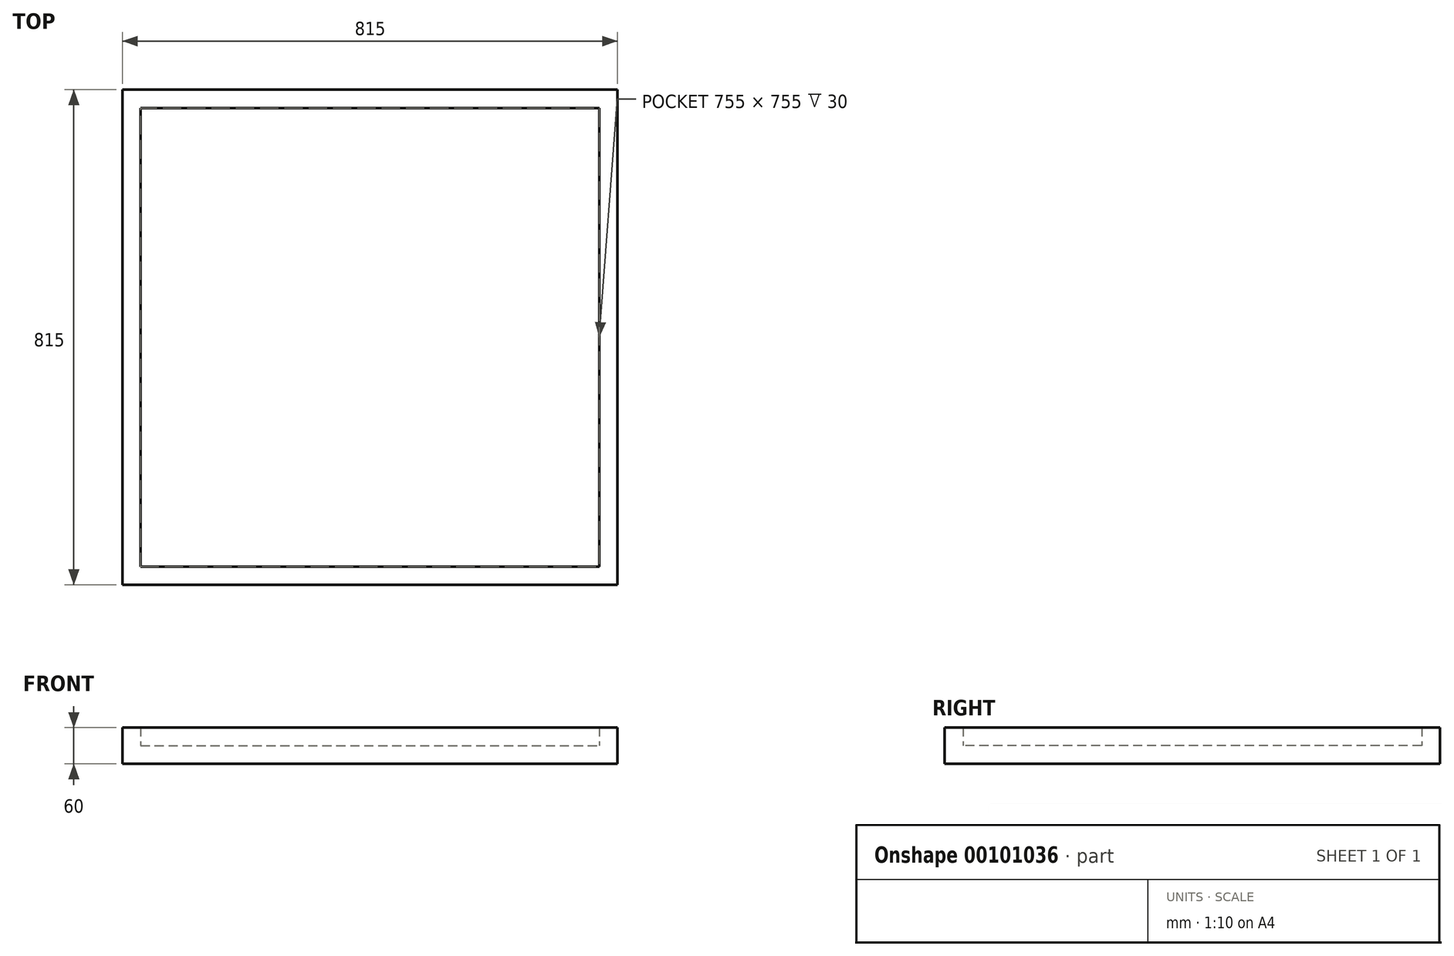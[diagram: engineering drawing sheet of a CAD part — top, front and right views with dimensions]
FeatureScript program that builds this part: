
annotation { "Feature Type Name" : "Feature", "Feature Type Description" : "" }
export const myFeature = defineFeature(function(context is Context, id is Id, definition is map)
    precondition{}
    {
        {
            var Q0;
            Q0=qCreatedBy(makeId("Top.planeOp"),FACE);
            var sketch = newSketch(context, id + "F0", { "sketchPlane" : qUnion([Q0])});
            skLineSegment(sketch, "E0.bottom", {"start": v(-369.35, 343.09) * mm, "end": v(385.65, 343.09) * mm});
            skLineSegment(sketch, "E0.top", {"start": v(-369.35, -411.91) * mm, "end": v(385.65, -411.91) * mm});
            skLineSegment(sketch, "E0.left", {"start": v(-369.35, 343.09) * mm, "end": v(-369.35, -411.91) * mm});
            skLineSegment(sketch, "E0.right", {"start": v(385.65, 343.09) * mm, "end": v(385.65, -411.91) * mm});
            skLineSegment(sketch, "E1.bottom", {"start": v(-399.35, 373.09) * mm, "end": v(415.65, 373.09) * mm});
            skLineSegment(sketch, "E1.top", {"start": v(-399.35, -441.91) * mm, "end": v(415.65, -441.91) * mm});
            skLineSegment(sketch, "E1.left", {"start": v(-399.35, 373.09) * mm, "end": v(-399.35, -441.91) * mm});
            skLineSegment(sketch, "E1.right", {"start": v(415.65, 373.09) * mm, "end": v(415.65, -441.91) * mm});
            skSolve(sketch);
        }
        {
            var Q0;
            Q0=makeQuery(id+"F0.imprint","IMPRINT",FACE,{"disambiguationData":[TD([[makeQuery(id+"F0.imprint","IMPRINT",EDGE,{"derivedFrom":sQuery(id+"F0.wireOp",EDGE,"E0.bottom")}),-1.0]])]});
            extrude(context, id + "F1", {"entities" : qUnion([Q0]), "depth" : 30 * mm});
        }
        {
            var Q0;
            Q0 = qSketchRegion(id + "F0", true);
            extrude(context, id + "F2", {"entities" : qUnion([Q0]), "operationType" : NewBodyOperationType.ADD, "depth" : 60 * mm});
        }
    });
